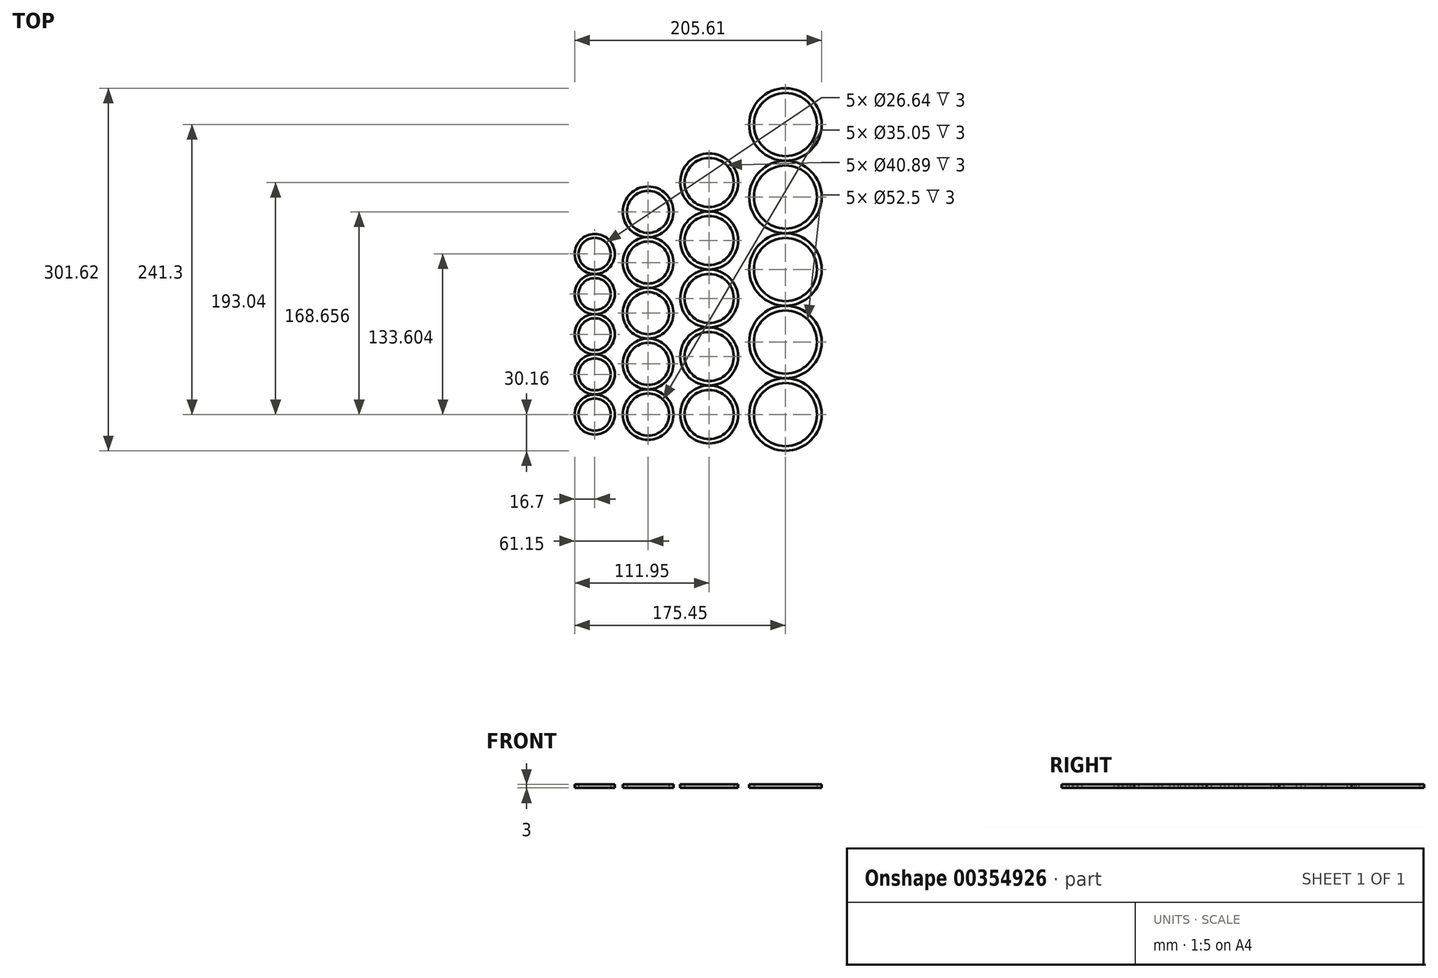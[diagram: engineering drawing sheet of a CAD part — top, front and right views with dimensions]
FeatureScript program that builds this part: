
annotation { "Feature Type Name" : "Feature", "Feature Type Description" : "" }
export const myFeature = defineFeature(function(context is Context, id is Id, definition is map)
    precondition{}
    {
        {
            assignVariable(context, id + "F0", {"name" : "th1", "anyValue" : 3});
        }
        {
            assignVariable(context, id + "F1", {"name" : "th2", "anyValue" : 6});
        }
        {
            assignVariable(context, id + "F2", {"name" : "th3", "anyValue" : 11.5});
        }
        {
            assignVariable(context, id + "F3", {"name" : "th4", "anyValue" : 23.5});
        }
        {
            assignVariable(context, id + "F4", {"name" : "th5", "anyValue" : 47.5});
        }
        {
            var Q0;
            Q0=qCreatedBy(makeId("Top.planeOp"),FACE);
            var sketch = newSketch(context, id + "F5", { "sketchPlane" : qUnion([Q0])});
            skCircle(sketch, "E0", {"center": v(0, 0) * mm, "radius": 20.45 * mm});
            skCircle(sketch, "E1", {"center": v(0, 0) * mm, "radius": 24.13 * mm});
            skCircle(sketch, "E2.0.1.0", {"center": v(0, 48.26) * mm, "radius": 24.13 * mm});
            skCircle(sketch, "E2.0.1.1", {"center": v(0, 48.26) * mm, "radius": 20.45 * mm});
            skCircle(sketch, "E2.0.2.0", {"center": v(0, 96.52) * mm, "radius": 24.13 * mm});
            skCircle(sketch, "E2.0.2.1", {"center": v(0, 96.52) * mm, "radius": 20.45 * mm});
            skCircle(sketch, "E2.0.3.0", {"center": v(0, 144.78) * mm, "radius": 24.13 * mm});
            skCircle(sketch, "E2.0.3.1", {"center": v(0, 144.78) * mm, "radius": 20.45 * mm});
            skLineSegment(sketch, "E2.direction1", {"start": v(0, 0) * mm, "end": v(27.94, 0) * mm, "construction": true});
            skLineSegment(sketch, "E2.direction2", {"start": v(0, 0) * mm, "end": v(0, 48.26) * mm, "construction": true});
            skCircle(sketch, "E3.0.0.4", {"center": v(0, 193.04) * mm, "radius": 24.13 * mm});
            skCircle(sketch, "E3.2.0.4", {"center": v(0, 193.04) * mm, "radius": 20.45 * mm});
            skCircle(sketch, "E4", {"center": v(63.5, 0) * mm, "radius": 26.25 * mm});
            skCircle(sketch, "E5", {"center": v(63.5, 0) * mm, "radius": 30.16 * mm});
            skCircle(sketch, "E6.0.1.0", {"center": v(63.5, 60.33) * mm, "radius": 30.16 * mm});
            skCircle(sketch, "E6.0.1.1", {"center": v(63.5, 60.33) * mm, "radius": 26.25 * mm});
            skCircle(sketch, "E6.0.2.0", {"center": v(63.5, 120.65) * mm, "radius": 30.16 * mm});
            skCircle(sketch, "E6.0.2.1", {"center": v(63.5, 120.65) * mm, "radius": 26.25 * mm});
            skCircle(sketch, "E6.0.3.0", {"center": v(63.5, 180.97) * mm, "radius": 30.16 * mm});
            skCircle(sketch, "E6.0.3.1", {"center": v(63.5, 180.97) * mm, "radius": 26.25 * mm});
            skCircle(sketch, "E6.0.4.0", {"center": v(63.5, 241.3) * mm, "radius": 30.16 * mm});
            skCircle(sketch, "E6.0.4.1", {"center": v(63.5, 241.3) * mm, "radius": 26.25 * mm});
            skLineSegment(sketch, "E6.direction1", {"start": v(63.5, 0) * mm, "end": v(88.9, 0) * mm, "construction": true});
            skLineSegment(sketch, "E6.direction2", {"start": v(63.5, 0) * mm, "end": v(63.5, 60.33) * mm, "construction": true});
            skCircle(sketch, "E7", {"center": v(-50.8, 0) * mm, "radius": 17.53 * mm});
            skCircle(sketch, "E8", {"center": v(-50.8, 0) * mm, "radius": 21.08 * mm});
            skCircle(sketch, "E9", {"center": v(-95.25, 0) * mm, "radius": 13.32 * mm});
            skCircle(sketch, "E10", {"center": v(-95.25, 0) * mm, "radius": 16.7 * mm});
            skCircle(sketch, "E11.0.1.0", {"center": v(-50.8, 42.16) * mm, "radius": 21.08 * mm});
            skCircle(sketch, "E11.0.1.1", {"center": v(-50.8, 42.16) * mm, "radius": 17.53 * mm});
            skCircle(sketch, "E11.0.2.0", {"center": v(-50.8, 84.33) * mm, "radius": 21.08 * mm});
            skCircle(sketch, "E11.0.2.1", {"center": v(-50.8, 84.33) * mm, "radius": 17.53 * mm});
            skCircle(sketch, "E11.0.3.0", {"center": v(-50.8, 126.5) * mm, "radius": 21.08 * mm});
            skCircle(sketch, "E11.0.3.1", {"center": v(-50.8, 126.5) * mm, "radius": 17.53 * mm});
            skCircle(sketch, "E11.0.4.0", {"center": v(-50.8, 168.66) * mm, "radius": 21.08 * mm});
            skCircle(sketch, "E11.0.4.1", {"center": v(-50.8, 168.66) * mm, "radius": 17.53 * mm});
            skLineSegment(sketch, "E11.direction1", {"start": v(-50.8, 0) * mm, "end": v(-25.4, 0) * mm, "construction": true});
            skLineSegment(sketch, "E11.direction2", {"start": v(-50.8, 0) * mm, "end": v(-50.8, 42.16) * mm, "construction": true});
            skCircle(sketch, "E12.0.1.0", {"center": v(-95.25, 33.4) * mm, "radius": 13.32 * mm});
            skCircle(sketch, "E12.0.1.1", {"center": v(-95.25, 33.4) * mm, "radius": 16.7 * mm});
            skCircle(sketch, "E12.0.2.0", {"center": v(-95.25, 66.8) * mm, "radius": 13.32 * mm});
            skCircle(sketch, "E12.0.2.1", {"center": v(-95.25, 66.8) * mm, "radius": 16.7 * mm});
            skCircle(sketch, "E12.0.3.0", {"center": v(-95.25, 100.2) * mm, "radius": 13.32 * mm});
            skCircle(sketch, "E12.0.3.1", {"center": v(-95.25, 100.2) * mm, "radius": 16.7 * mm});
            skCircle(sketch, "E12.0.4.0", {"center": v(-95.25, 133.6) * mm, "radius": 13.32 * mm});
            skCircle(sketch, "E12.0.4.1", {"center": v(-95.25, 133.6) * mm, "radius": 16.7 * mm});
            skLineSegment(sketch, "E12.direction1", {"start": v(-95.25, 0) * mm, "end": v(-69.85, 0) * mm, "construction": true});
            skLineSegment(sketch, "E12.direction2", {"start": v(-95.25, 0) * mm, "end": v(-95.25, 33.4) * mm, "construction": true});
            skSolve(sketch);
        }
        {
            var Q0;
            Q0 = qSketchRegion(id + "F5", true);
            extrude(context, id + "F6", {"entities" : qUnion([Q0]), "depth" : (getVariable(context, 'th1')) * mm});
        }
        {
            var Q0;
            Q0=sQuery(id+"F5.wireOp",EDGE,"E2.0.1.0");
            var Q1;
            Q1=sQuery(id+"F5.wireOp",EDGE,"E2.0.1.1");
            var Q2;
            Q2=sQuery(id+"F5.wireOp",EDGE,"E11.0.1.0");
            var Q3;
            Q3=sQuery(id+"F5.wireOp",EDGE,"E11.0.1.1");
            var Q4;
            Q4=sQuery(id+"F5.wireOp",EDGE,"E12.0.1.1");
            var Q5;
            Q5=sQuery(id+"F5.wireOp",EDGE,"E12.0.1.0");
            var Q6;
            Q6=sQuery(id+"F5.wireOp",EDGE,"E6.0.1.1");
            var Q7;
            Q7=sQuery(id+"F5.wireOp",EDGE,"E6.0.1.0");
            extrude(context, id + "F7", {"bodyType" : ToolBodyType.SURFACE, "surfaceEntities" : qUnion([Q0, Q1, Q2, Q3, Q4, Q5, Q6, Q7]), "depth" : (getVariable(context, 'th2')) * mm});
        }
        {
            var Q0;
            Q0=sQuery(id+"F5.wireOp",EDGE,"E2.0.2.0");
            var Q1;
            Q1=sQuery(id+"F5.wireOp",EDGE,"E2.0.2.1");
            var Q2;
            Q2=sQuery(id+"F5.wireOp",EDGE,"E6.0.2.1");
            var Q3;
            Q3=sQuery(id+"F5.wireOp",EDGE,"E6.0.2.0");
            var Q4;
            Q4=sQuery(id+"F5.wireOp",EDGE,"E11.0.2.1");
            var Q5;
            Q5=sQuery(id+"F5.wireOp",EDGE,"E11.0.2.0");
            var Q6;
            Q6=sQuery(id+"F5.wireOp",EDGE,"E12.0.2.0");
            var Q7;
            Q7=sQuery(id+"F5.wireOp",EDGE,"E12.0.2.1");
            extrude(context, id + "F8", {"bodyType" : ToolBodyType.SURFACE, "surfaceEntities" : qUnion([Q0, Q1, Q2, Q3, Q4, Q5, Q6, Q7]), "depth" : (getVariable(context, 'th3')) * mm});
        }
        {
            var Q0;
            Q0=sQuery(id+"F5.wireOp",EDGE,"E2.0.3.0");
            var Q1;
            Q1=sQuery(id+"F5.wireOp",EDGE,"E2.0.3.1");
            var Q2;
            Q2=sQuery(id+"F5.wireOp",EDGE,"E6.0.3.1");
            var Q3;
            Q3=sQuery(id+"F5.wireOp",EDGE,"E6.0.3.0");
            var Q4;
            Q4=sQuery(id+"F5.wireOp",EDGE,"E11.0.3.1");
            var Q5;
            Q5=sQuery(id+"F5.wireOp",EDGE,"E12.0.3.0");
            var Q6;
            Q6=sQuery(id+"F5.wireOp",EDGE,"E12.0.3.1");
            extrude(context, id + "F9", {"bodyType" : ToolBodyType.SURFACE, "surfaceEntities" : qUnion([Q0, Q1, Q2, Q3, Q4, Q5, Q6]), "depth" : (getVariable(context, 'th4')) * mm});
        }
        {
            var Q0;
            Q0=sQuery(id+"F5.wireOp",EDGE,"E3.0.0.4");
            var Q1;
            Q1=sQuery(id+"F5.wireOp",EDGE,"E3.2.0.4");
            var Q2;
            Q2=sQuery(id+"F5.wireOp",EDGE,"E6.0.4.0");
            var Q3;
            Q3=sQuery(id+"F5.wireOp",EDGE,"E6.0.4.1");
            var Q4;
            Q4=sQuery(id+"F5.wireOp",EDGE,"E11.0.4.0");
            var Q5;
            Q5=sQuery(id+"F5.wireOp",EDGE,"E11.0.4.1");
            var Q6;
            Q6=sQuery(id+"F5.wireOp",EDGE,"E12.0.4.1");
            var Q7;
            Q7=sQuery(id+"F5.wireOp",EDGE,"E12.0.4.0");
            extrude(context, id + "F10", {"bodyType" : ToolBodyType.SURFACE, "surfaceEntities" : qUnion([Q0, Q1, Q2, Q3, Q4, Q5, Q6, Q7]), "depth" : (getVariable(context, 'th5')) * mm});
        }
    });
